# Revit family: Shower-Shower_Arm-KOHLER-K-15396BR_1
name_source: partatom
category: Plumbing Fixtures
revit_build: Autodesk Revit 2017 (Build: 20160225_1515(x64)
units: mm (PartAtom-declared; Revit-internal decimal feet)

## family parameters
Cut with Voids When Loaded = No
Host = Face
OmniClass Number = 23.31.25.00
OmniClass Title = Toilet and Bath Specialties
Part Type = Normal
Room Calculation Point = No
Round Connector Dimension = Use Diameter
Shared = No

## types (6) — shared parameters
ADA Compliant = No
Assembly Code = D2010700
CW Connection = No
Cold Water Inlet = Cold Water Inlet
Date Modified = 09/07/2021
Default Elevation = 72"
Description = WALL MOUNT SHOWER ARM, 15 INCH
Drain Included = No
Flow Rate = 0 GPM
HW Connection = Yes
Height = 4 1/16"
Hot Water Inlet = Hot Water Inlet
Length = 13 7/8"
Manufacturer = KOHLER Co.
Master Format 2014 = 22 42 23
Master Format 2014 Name = Residential Showers
Material = Brass Construction
Pressure = 0.00 psi
Tempered Water Inlet = Tempered Water Inlet
URL = https://br.kohler.com
Vent Connection = No
Waste Connection = No
Waste Water Outlet = Waste Water Outlet
WaterSense Certified = No
Width = 2 9/16"

## per-type parameters (varying)
| type | Finish | Model | Type |
| CP- Polished Chrome | Kohler-Metal-CP-Polished_Chrome | K-15396BR-CP | 1 |
| BN- Vibrant Brushed Nickel | Kohler-Metal-BN-Vibrant_Brushed_Nickel | K-15396BR-BN | 2 |
| BL- Matte Black | Kohler-Metal-BL-Matte_Black | K-15396BR-BL | 3 |
| RGD- Polished Rose Gold | Kohler-Metal-RGD-Polished_Rose_Gold | K-15396BR-RGD | 4 |
| SN- Vibrant Polished Nickel | Kohler-Metal-SN-Vibrant_Polished_Nickel | K-15396BR-SN | 5 |
| TT- Vibrant Titanium | Kohler-Metal-TT-Vibrant_Titanium | K-15396BR-TT | 6 |

## geometry (parser evidence)
native form markers: Sweep x6
no freeform markers — native parametric forms only
